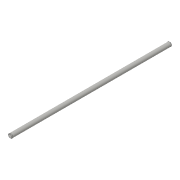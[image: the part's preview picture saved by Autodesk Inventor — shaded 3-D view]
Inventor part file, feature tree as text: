
AUTODESK INVENTOR PART (.ipt)
format: ipt  version: 2016 (Build 200138000, 138)  size: 71,680 bytes
history: native  units: in
note: dims shown in document units (in); Inventor stores cm internally (conversion verified against a paired STEP export)
features: other x1, extrude x1, chamfer x1, sketch x1
ambient origin geometry x8: Origin, YZ Plane, XZ Plane, XY Plane, X Axis, Y Axis, Z Axis, Center Point
bodies: Solid1 (feature_tree)
feature tree (4):
  other  "skeleton.ipt"
  extrude  "Extrusion1"  Depth=11.811in TaperAngle=0.0deg
  chamfer  "Chamfer1"  Distance=0.3937in
  sketch  "Sketch1"  dims[d0=0.315in d1=11.811in d2=0.0in d3=0.3937in d4=0.0394in d5=0.0787in d6=45.0deg]
